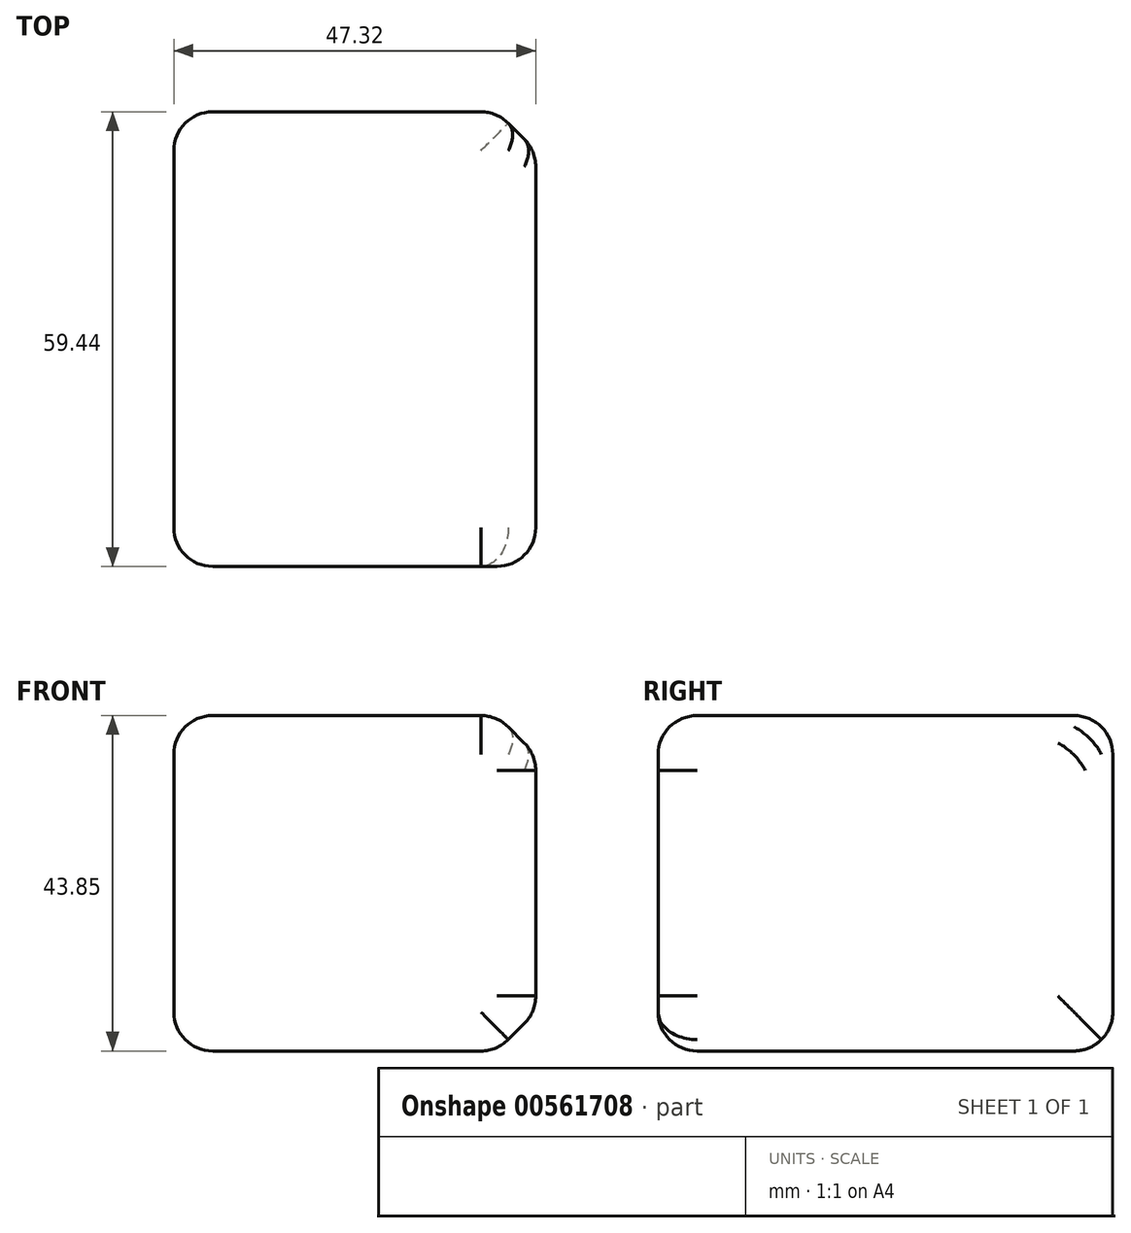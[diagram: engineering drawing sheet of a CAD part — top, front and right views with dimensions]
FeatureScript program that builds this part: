
annotation { "Feature Type Name" : "Feature", "Feature Type Description" : "" }
export const myFeature = defineFeature(function(context is Context, id is Id, definition is map)
    precondition{}
    {
        {
            var Q0;
            Q0=qCreatedBy(makeId("Front.planeOp"),FACE);
            var sketch = newSketch(context, id + "F0", { "sketchPlane" : qUnion([Q0])});
            skLineSegment(sketch, "E0.bottom", {"start": v(0, 0) * mm, "end": v(47.32, 0) * mm});
            skLineSegment(sketch, "E0.top", {"start": v(0, 43.85) * mm, "end": v(47.32, 43.85) * mm});
            skLineSegment(sketch, "E0.left", {"start": v(0, 0) * mm, "end": v(0, 43.85) * mm});
            skLineSegment(sketch, "E0.right", {"start": v(47.32, 0) * mm, "end": v(47.32, 43.85) * mm});
            skSolve(sketch);
        }
        {
            var Q0;
            Q0=makeQuery(id+"F0.imprint","IMPRINT",FACE,{"disambiguationData":[TD([[makeQuery(id+"F0.imprint","IMPRINT",EDGE,{"derivedFrom":sQuery(id+"F0.wireOp",EDGE,"E0.bottom")}),1.0]])]});
            extrude(context, id + "F1", {"entities" : qUnion([Q0]), "depth" : 59.44 * mm, "offsetDistance" : 25.4 * mm});
        }
        {
            var Q0;
            Q0=makeQuery(id+"F1.opExtrude","CAP_FACE",FACE,{"disambiguationData":[OSD([sQuery(id+"F0.wireOp",EDGE,"E0.bottom"),sQuery(id+"F0.wireOp",EDGE,"E0.top"),sQuery(id+"F0.wireOp",EDGE,"E0.left"),sQuery(id+"F0.wireOp",EDGE,"E0.right")])],"isStart":false});
            fillet(context, id + "F2", {"entities" : qUnion([Q0]), "radius" : 5.08 * mm, "tangentPropagation" : true, "allowEdgeOverflow" : false});
        }
        {
            var Q0;
            Q0=makeQuery(id+"F1.opExtrude","SWEPT_FACE",FACE,{"disambiguationData":[OSD([sQuery(id+"F0.wireOp",EDGE,"E0.right")])]});
            chamfer(context, id + "F3", {"entities" : qUnion([Q0]), "width" : 5.08 * mm, "tangentPropagation" : true});
        }
        {
            var Q0;
            Q0=makeQuery(id+"F3.opChamfer","BLEND_FACE",FACE,{"disambiguationData":[OSD([sQuery(id+"F0.wireOp",EDGE,"E0.top"),sQuery(id+"F0.wireOp",EDGE,"E0.right")])]});
            var Q1;
            Q1=makeQuery(id+"F1.opExtrude","SWEPT_FACE",FACE,{"disambiguationData":[OSD([sQuery(id+"F0.wireOp",EDGE,"E0.right")])]});
            fillet(context, id + "F4", {"entities" : qUnion([Q0, Q1]), "radius" : 5.08 * mm, "tangentPropagation" : true, "allowEdgeOverflow" : false});
        }
        {
            var Q0;
            Q0=makeQuery(id+"F1.opExtrude","SWEPT_FACE",FACE,{"disambiguationData":[OSD([sQuery(id+"F0.wireOp",EDGE,"E0.top")])]});
            fillet(context, id + "F5", {"entities" : qUnion([Q0]), "radius" : 5.08 * mm, "tangentPropagation" : true, "allowEdgeOverflow" : false});
        }
        {
            var Q0;
            Q0=makeQuery(id+"F1.opExtrude","CAP_FACE",FACE,{"disambiguationData":[OSD([sQuery(id+"F0.wireOp",EDGE,"E0.bottom"),sQuery(id+"F0.wireOp",EDGE,"E0.top"),sQuery(id+"F0.wireOp",EDGE,"E0.left"),sQuery(id+"F0.wireOp",EDGE,"E0.right")])],"isStart":true});
            fillet(context, id + "F6", {"entities" : qUnion([Q0]), "radius" : 5.08 * mm, "tangentPropagation" : true, "allowEdgeOverflow" : false});
        }
        {
            var Q0;
            Q0=makeQuery(id+"F1.opExtrude","SWEPT_FACE",FACE,{"disambiguationData":[OSD([sQuery(id+"F0.wireOp",EDGE,"E0.left")])]});
            fillet(context, id + "F7", {"entities" : qUnion([Q0]), "radius" : 5.08 * mm, "tangentPropagation" : true, "allowEdgeOverflow" : false});
        }
        {
            var Q0;
            Q0=makeQuery(id+"F1.opExtrude","SWEPT_FACE",FACE,{"disambiguationData":[OSD([sQuery(id+"F0.wireOp",EDGE,"E0.bottom")])]});
            fillet(context, id + "F8", {"entities" : qUnion([Q0]), "radius" : 5.08 * mm, "tangentPropagation" : true, "allowEdgeOverflow" : false});
        }
    });
